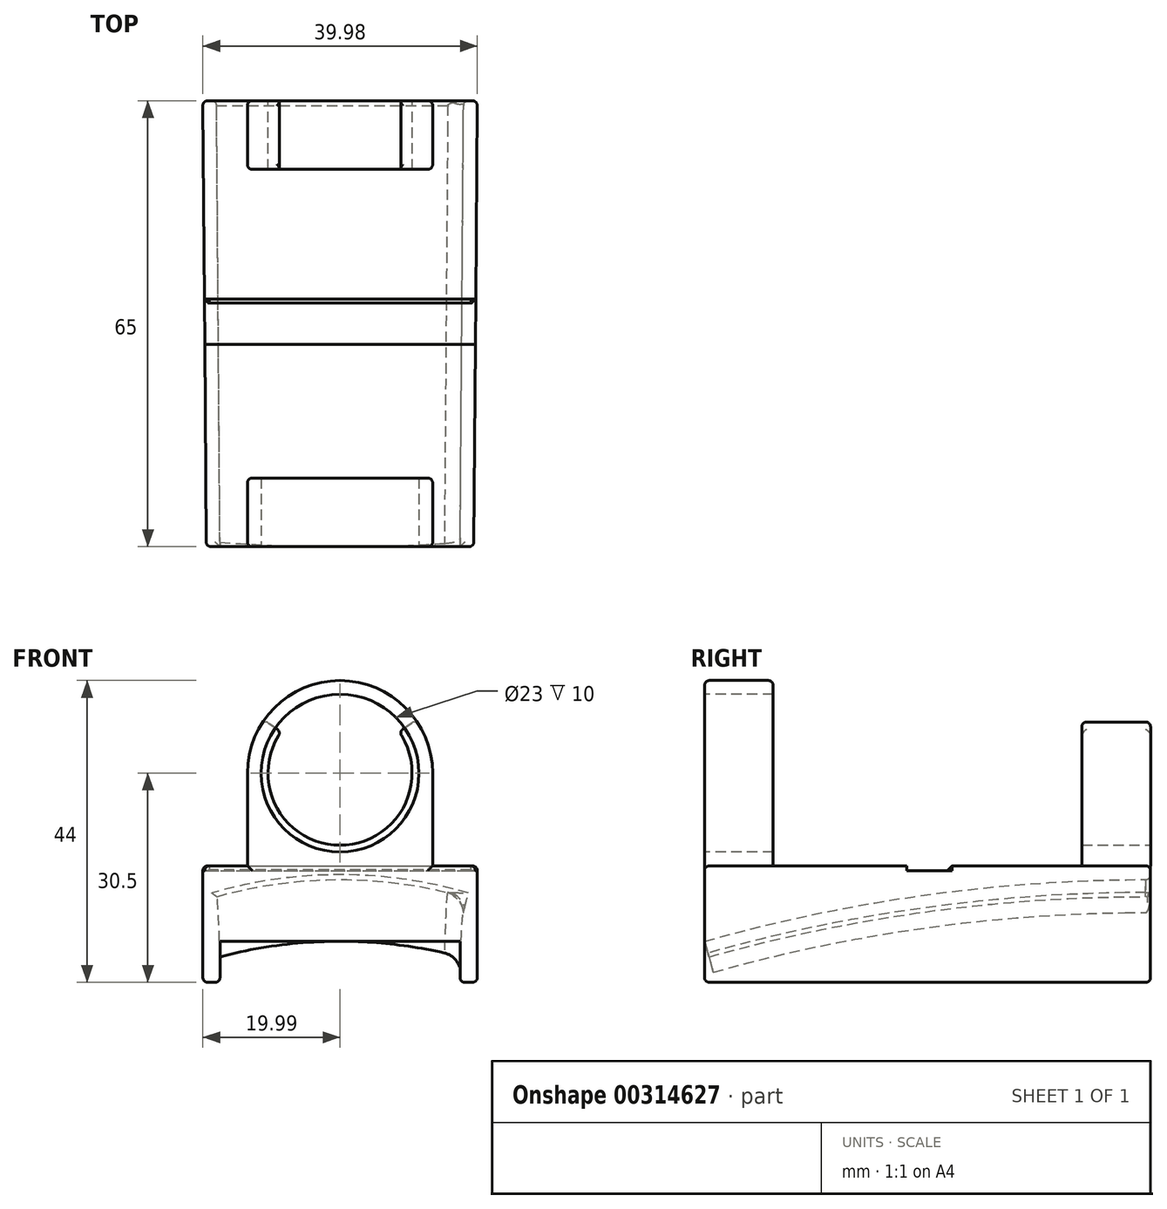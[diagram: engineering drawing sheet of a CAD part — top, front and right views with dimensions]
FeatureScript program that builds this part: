
annotation { "Feature Type Name" : "Feature", "Feature Type Description" : "" }
export const myFeature = defineFeature(function(context is Context, id is Id, definition is map)
    precondition{}
    {
        {
            assignVariable(context, id + "F0", {"name" : "var_thickness", "anyValue" : 2});
        }
        {
            var Q0;
            Q0=qCreatedBy(makeId("Top.planeOp"),FACE);
            var sketch = newSketch(context, id + "F1", { "sketchPlane" : qUnion([Q0])});
            skLineSegment(sketch, "E0.bottom", {"start": v(-20, 32.5) * mm, "end": v(20, 32.5) * mm});
            skLineSegment(sketch, "E0.top", {"start": v(-19.5, -32.5) * mm, "end": v(19.5, -32.5) * mm});
            skLineSegment(sketch, "E0.left", {"start": v(-20, 32.5) * mm, "end": v(-19.5, -32.5) * mm});
            skLineSegment(sketch, "E0.right", {"start": v(20, 32.5) * mm, "end": v(19.5, -32.5) * mm});
            skSolve(sketch);
        }
        {
            var Q0;
            Q0 = qSketchRegion(id + "F1", true);
            extrude(context, id + "F2", {"entities" : qUnion([Q0]), "depth" : 2 * mm});
        }
        {
            var Q0;
            Q0=makeQuery(id+"F2.opExtrude","CAP_FACE",FACE,{"disambiguationData":[OSD([sQuery(id+"F1.wireOp",EDGE,"E0.bottom"),sQuery(id+"F1.wireOp",EDGE,"E0.top"),sQuery(id+"F1.wireOp",EDGE,"E0.left"),sQuery(id+"F1.wireOp",EDGE,"E0.right")])],"isStart":true});
            var sketch = newSketch(context, id + "F3", { "sketchPlane" : qUnion([Q0])});
            skLineSegment(sketch, "E1", {"start": v(20, -32.5) * mm, "end": v(19.5, 32.5) * mm});
            skLineSegment(sketch, "E2", {"start": v(19.5, 32.5) * mm, "end": v(17.5, 32.5) * mm});
            skLineSegment(sketch, "E3", {"start": v(17.5, 32.5) * mm, "end": v(18, -32.5) * mm});
            skLineSegment(sketch, "E4", {"start": v(18, -32.5) * mm, "end": v(20, -32.5) * mm});
            skLineSegment(sketch, "E5", {"start": v(0, -32.5) * mm, "end": v(0, 32.5) * mm, "construction": true});
            skLineSegment(sketch, "E6.MirrorCS", {"start": v(-18, -32.5) * mm, "end": v(-20, -32.5) * mm});
            skLineSegment(sketch, "E7.MirrorCS", {"start": v(-17.5, 32.5) * mm, "end": v(-18, -32.5) * mm});
            skLineSegment(sketch, "E8.MirrorCS", {"start": v(-20, -32.5) * mm, "end": v(-19.5, 32.5) * mm});
            skLineSegment(sketch, "E9.MirrorCS", {"start": v(-19.5, 32.5) * mm, "end": v(-17.5, 32.5) * mm});
            skSolve(sketch);
        }
        {
            var Q0;
            Q0 = qSketchRegion(id + "F3", true);
            extrude(context, id + "F4", {"entities" : qUnion([Q0]), "operationType" : NewBodyOperationType.ADD, "depth" : 15 * mm});
        }
        {
            var Q0;
            Q0=makeQuery(id+"F2.opExtrude","CAP_FACE",FACE,{"disambiguationData":[OSD([sQuery(id+"F1.wireOp",EDGE,"E0.bottom"),sQuery(id+"F1.wireOp",EDGE,"E0.top"),sQuery(id+"F1.wireOp",EDGE,"E0.left"),sQuery(id+"F1.wireOp",EDGE,"E0.right")])],"isStart":false});
            var sketch = newSketch(context, id + "F5", { "sketchPlane" : qUnion([Q0])});
            skLineSegment(sketch, "E10.bottom", {"start": v(-13.5, -32.5) * mm, "end": v(13.5, -32.5) * mm});
            skLineSegment(sketch, "E10.top", {"start": v(-13.5, -22.5) * mm, "end": v(13.5, -22.5) * mm});
            skLineSegment(sketch, "E10.left", {"start": v(-13.5, -32.5) * mm, "end": v(-13.5, -22.5) * mm});
            skLineSegment(sketch, "E10.right", {"start": v(13.5, -32.5) * mm, "end": v(13.5, -22.5) * mm});
            skLineSegment(sketch, "E11.bottom", {"start": v(-13.5, 32.5) * mm, "end": v(13.5, 32.5) * mm});
            skLineSegment(sketch, "E11.top", {"start": v(-13.5, 22.5) * mm, "end": v(13.5, 22.5) * mm});
            skLineSegment(sketch, "E11.left", {"start": v(-13.5, 32.5) * mm, "end": v(-13.5, 22.5) * mm});
            skLineSegment(sketch, "E11.right", {"start": v(13.5, 32.5) * mm, "end": v(13.5, 22.5) * mm});
            skSolve(sketch);
        }
        {
            var Q0;
            Q0 = qSketchRegion(id + "F5", true);
            extrude(context, id + "F6", {"entities" : qUnion([Q0]), "operationType" : NewBodyOperationType.ADD, "depth" : (25 + getVariable(context, 'var_thickness')) * mm});
        }
        {
            var Q0;
            Q0=makeQuery(id+"F6.opExtrude","CAP_EDGE",EDGE,{"disambiguationData":[OSD([sQuery(id+"F5.wireOp",EDGE,"E10.right")])],"isStart":false});
            var Q1;
            Q1=makeQuery(id+"F6.opExtrude","CAP_EDGE",EDGE,{"disambiguationData":[OSD([sQuery(id+"F5.wireOp",EDGE,"E10.left")])],"isStart":false});
            var Q2;
            Q2=makeQuery(id+"F6.opExtrude","CAP_EDGE",EDGE,{"disambiguationData":[OSD([sQuery(id+"F5.wireOp",EDGE,"E11.right")])],"isStart":false});
            var Q3;
            Q3=makeQuery(id+"F6.opExtrude","CAP_EDGE",EDGE,{"disambiguationData":[OSD([sQuery(id+"F5.wireOp",EDGE,"E11.left")])],"isStart":false});
            fillet(context, id + "F7", {"entities" : qUnion([Q0, Q1, Q2, Q3]), "radius" : (11.5 + getVariable(context, 'var_thickness')) * mm, "tangentPropagation" : true, "allowEdgeOverflow" : false});
        }
        {
            var Q0;
            Q0=makeQuery(id+"F6.boolean.opBoolean","MERGE",FACE,{"derivedFrom":[makeQuery(id+"F4.boolean.opBoolean","MERGE",FACE,{"derivedFrom":[makeQuery(id+"F2.opExtrude","SWEPT_FACE",FACE,{"disambiguationData":[OSD([sQuery(id+"F1.wireOp",EDGE,"E0.top")])]}),makeQuery(id+"F4.opExtrude","SWEPT_FACE",FACE,{"disambiguationData":[OSD([sQuery(id+"F3.wireOp",EDGE,"E2")])]}),makeQuery(id+"F4.opExtrude","SWEPT_FACE",FACE,{"disambiguationData":[OSD([sQuery(id+"F3.wireOp",EDGE,"E9.MirrorCS")])]})]}),makeQuery(id+"F6.opExtrude","SWEPT_FACE",FACE,{"disambiguationData":[OSD([sQuery(id+"F5.wireOp",EDGE,"E10.bottom")])]})]});
            var sketch = newSketch(context, id + "F8", { "sketchPlane" : qUnion([Q0])});
            skCircle(sketch, "E12", {"center": v(0, 15.5) * mm, "radius": 11.5 * mm});
            skSolve(sketch);
        }
        {
            var Q0;
            Q0 = qSketchRegion(id + "F8", true);
            var Q1;
            Q1=makeQuery(id+"F6.opExtrude","SWEPT_FACE",FACE,{"disambiguationData":[OSD([sQuery(id+"F5.wireOp",EDGE,"E10.top")])]});
            var Q2;
            Q2=makeQuery(id+"F6.opExtrude","SWEPT_FACE",FACE,{"disambiguationData":[OSD([sQuery(id+"F5.wireOp",EDGE,"E10.top")])]});
            extrude(context, id + "F9", {"entities" : qUnion([Q0, Q1]), "operationType" : NewBodyOperationType.REMOVE, "endBound" : BoundingType.UP_TO_NEXT, "oppositeDirection" : true, "endBoundEntityFace" : qUnion([Q2]), "depth" : 25 * mm});
        }
        {
            var Q0;
            Q0=makeQuery(id+"F6.opExtrude","SWEPT_FACE",FACE,{"disambiguationData":[OSD([sQuery(id+"F5.wireOp",EDGE,"E11.bottom")])]});
            var sketch = newSketch(context, id + "F10", { "sketchPlane" : qUnion([Q0])});
            skCircle(sketch, "E13", {"center": v(0, 15.5) * mm, "radius": 10.5 * mm});
            skSolve(sketch);
        }
        {
            var Q0;
            Q0 = qSketchRegion(id + "F10", true);
            extrude(context, id + "F11", {"entities" : qUnion([Q0]), "operationType" : NewBodyOperationType.REMOVE, "endBound" : BoundingType.UP_TO_NEXT, "oppositeDirection" : true, "depth" : 25 * mm});
        }
        {
            var Q0;
            Q0=makeQuery(id+"F6.opExtrude","SWEPT_FACE",FACE,{"disambiguationData":[OSD([sQuery(id+"F5.wireOp",EDGE,"E11.bottom")])]});
            var sketch = newSketch(context, id + "F12", { "sketchPlane" : qUnion([Q0])});
            skArc(sketch, "E14", {"start": v(4.1, 18.37) * mm, "mid": v(0, 20.5) * mm, "end": v(-4.1, 18.37) * mm});
            skArc(sketch, "E15", {"start": v(12.29, 24.1) * mm, "mid": v(0, 30.5) * mm, "end": v(-12.29, 24.1) * mm});
            skLineSegment(sketch, "E16", {"start": v(4.1, 18.37) * mm, "end": v(12.29, 24.1) * mm});
            skLineSegment(sketch, "E17", {"start": v(-12.29, 24.1) * mm, "end": v(-4.1, 18.37) * mm});
            skSolve(sketch);
        }
        {
            var Q0;
            Q0 = qSketchRegion(id + "F12", true);
            var Q1;
            Q1=makeQuery(id+"F6.opExtrude","SWEPT_FACE",FACE,{"disambiguationData":[OSD([sQuery(id+"F5.wireOp",EDGE,"E11.top")])]});
            extrude(context, id + "F13", {"entities" : qUnion([Q0]), "operationType" : NewBodyOperationType.REMOVE, "endBound" : BoundingType.UP_TO_SURFACE, "oppositeDirection" : true, "endBoundEntityFace" : qUnion([Q1]), "depth" : 25 * mm});
        }
        {
            var Q0;
            Q0=qCreatedBy(makeId("Right.planeOp"),FACE);
            var sketch = newSketch(context, id + "F14", { "sketchPlane" : qUnion([Q0])});
            skLineSegment(sketch, "E18", {"start": v(32.5, 0) * mm, "end": v(-32.5, 0) * mm});
            skLineSegment(sketch, "E19", {"start": v(-32.5, 0) * mm, "end": v(-32.5, -9) * mm});
            skArc(sketch, "E20", {"start": v(32.5, 0) * mm, "mid": v(-0.31, -2.26) * mm, "end": v(-32.5, -9) * mm});
            skSolve(sketch);
        }
        {
            var Q0;
            Q0 = qSketchRegion(id + "F14", true);
            extrude(context, id + "F15", {"entities" : qUnion([Q0]), "operationType" : NewBodyOperationType.ADD, "endBound" : BoundingType.SYMMETRIC, "depth" : 37 * mm});
        }
        {
            var Q0;
            Q0=qCreatedBy(makeId("Right.planeOp"),FACE);
            var sketch = newSketch(context, id + "F16", { "sketchPlane" : qUnion([Q0])});
            skArc(sketch, "E21", {"start": v(32.5, 0) * mm, "mid": v(-0.31, -2.26) * mm, "end": v(-32.5, -9) * mm});
            skSolve(sketch);
        }
        {
            var Q0;
            Q0=makeQuery(id+"F4.boolean.opBoolean","MERGE",FACE,{"derivedFrom":[makeQuery(id+"F2.opExtrude","SWEPT_FACE",FACE,{"disambiguationData":[OSD([sQuery(id+"F1.wireOp",EDGE,"E0.bottom")])]}),makeQuery(id+"F4.opExtrude","SWEPT_FACE",FACE,{"disambiguationData":[OSD([sQuery(id+"F3.wireOp",EDGE,"E4")])]}),makeQuery(id+"F4.opExtrude","SWEPT_FACE",FACE,{"disambiguationData":[OSD([sQuery(id+"F3.wireOp",EDGE,"E6.MirrorCS")])]})]});
            var sketch = newSketch(context, id + "F17", { "sketchPlane" : qUnion([Q0])});
            skLineSegment(sketch, "E22", {"start": v(18, -2.5) * mm, "end": v(18, 0) * mm});
            skLineSegment(sketch, "E23", {"start": v(18, 0) * mm, "end": v(-18, 0) * mm});
            skLineSegment(sketch, "E24", {"start": v(-18, 0) * mm, "end": v(-18, -2.5) * mm});
            skArc(sketch, "E25", {"start": v(18, -2.5) * mm, "mid": v(0, 0) * mm, "end": v(-18, -2.5) * mm});
            skSolve(sketch);
        }
        {
            var Q0;
            Q0 = qSketchRegion(id + "F17", true);
            var Q1;
            Q1=sQuery(id+"F16.wireOp",EDGE,"E21");
            sweep(context, id + "F18", {"operationType" : NewBodyOperationType.ADD, "profiles" : qUnion([Q0]), "path" : qUnion([Q1])});
        }
        {
            var Q0;
            Q0=qCreatedBy(makeId("Right.planeOp"),FACE);
            var sketch = newSketch(context, id + "F19", { "sketchPlane" : qUnion([Q0])});
            skLineSegment(sketch, "E26.bottom", {"start": v(-3, 2) * mm, "end": v(3, 2) * mm});
            skLineSegment(sketch, "E26.top", {"start": v(-3, 1.25) * mm, "end": v(3, 1.25) * mm});
            skLineSegment(sketch, "E26.left", {"start": v(-3, 2) * mm, "end": v(-3, 1.25) * mm});
            skLineSegment(sketch, "E26.right", {"start": v(3, 2) * mm, "end": v(3, 1.25) * mm});
            skSolve(sketch);
        }
        {
            var Q0;
            Q0 = qSketchRegion(id + "F19", true);
            extrude(context, id + "F20", {"entities" : qUnion([Q0]), "operationType" : NewBodyOperationType.REMOVE, "endBound" : BoundingType.SYMMETRIC, "oppositeDirection" : true, "depth" : 50 * mm});
        }
        {
            var Q0;
            Q0=makeQuery(id+"F4.opExtrude","CAP_FACE",FACE,{"disambiguationData":[OSD([sQuery(id+"F3.wireOp",EDGE,"E1"),sQuery(id+"F3.wireOp",EDGE,"E2"),sQuery(id+"F3.wireOp",EDGE,"E3"),sQuery(id+"F3.wireOp",EDGE,"E4")])],"isStart":false});
            var Q1;
            Q1=makeQuery(id+"F4.opExtrude","CAP_FACE",FACE,{"disambiguationData":[OSD([sQuery(id+"F3.wireOp",EDGE,"E6.MirrorCS"),sQuery(id+"F3.wireOp",EDGE,"E7.MirrorCS"),sQuery(id+"F3.wireOp",EDGE,"E8.MirrorCS"),sQuery(id+"F3.wireOp",EDGE,"E9.MirrorCS")])],"isStart":false});
            var Q2;
            Q2=makeQuery(id+"F7.opFillet","BLEND_EDGE",EDGE,{"blendedFrom":[makeQuery(id+"F6.opExtrude","CAP_EDGE",EDGE,{"disambiguationData":[OSD([sQuery(id+"F5.wireOp",EDGE,"E10.left")])],"isStart":false}),makeQuery(id+"F6.boolean.opBoolean","MERGE",FACE,{"derivedFrom":[makeQuery(id+"F4.boolean.opBoolean","MERGE",FACE,{"derivedFrom":[makeQuery(id+"F2.opExtrude","SWEPT_FACE",FACE,{"disambiguationData":[OSD([sQuery(id+"F1.wireOp",EDGE,"E0.top")])]}),makeQuery(id+"F4.opExtrude","SWEPT_FACE",FACE,{"disambiguationData":[OSD([sQuery(id+"F3.wireOp",EDGE,"E2")])]}),makeQuery(id+"F4.opExtrude","SWEPT_FACE",FACE,{"disambiguationData":[OSD([sQuery(id+"F3.wireOp",EDGE,"E9.MirrorCS")])]})]}),makeQuery(id+"F6.opExtrude","SWEPT_FACE",FACE,{"disambiguationData":[OSD([sQuery(id+"F5.wireOp",EDGE,"E10.bottom")])]})]})],"blendedInto":[makeQuery(id+"F6.boolean.opBoolean","MERGE",FACE,{"derivedFrom":[makeQuery(id+"F4.boolean.opBoolean","MERGE",FACE,{"derivedFrom":[makeQuery(id+"F2.opExtrude","SWEPT_FACE",FACE,{"disambiguationData":[OSD([sQuery(id+"F1.wireOp",EDGE,"E0.top")])]}),makeQuery(id+"F4.opExtrude","SWEPT_FACE",FACE,{"disambiguationData":[OSD([sQuery(id+"F3.wireOp",EDGE,"E2")])]}),makeQuery(id+"F4.opExtrude","SWEPT_FACE",FACE,{"disambiguationData":[OSD([sQuery(id+"F3.wireOp",EDGE,"E9.MirrorCS")])]})]}),makeQuery(id+"F6.opExtrude","SWEPT_FACE",FACE,{"disambiguationData":[OSD([sQuery(id+"F5.wireOp",EDGE,"E10.bottom")])]})]})]});
            var Q3;
            Q3=makeQuery(id+"F7.opFillet","BLEND_EDGE",EDGE,{"blendedFrom":[makeQuery(id+"F6.opExtrude","CAP_EDGE",EDGE,{"disambiguationData":[OSD([sQuery(id+"F5.wireOp",EDGE,"E10.left")])],"isStart":false}),makeQuery(id+"F6.opExtrude","SWEPT_FACE",FACE,{"disambiguationData":[OSD([sQuery(id+"F5.wireOp",EDGE,"E10.top")])]})],"blendedInto":[makeQuery(id+"F6.opExtrude","SWEPT_FACE",FACE,{"disambiguationData":[OSD([sQuery(id+"F5.wireOp",EDGE,"E10.top")])]})]});
            var Q4;
            {var subQ0=sQuery(id+"F1.wireOp",EDGE,"E0.right");var subQ1=sQuery(id+"F1.wireOp",EDGE,"E0.top");Q4=makeQuery(id+"F6.boolean.opBoolean","SPLIT",EDGE,{"disambiguationData":[TD([makeQuery(id+"F2.opExtrude","SWEPT_FACE",FACE,{"disambiguationData":[OSD([subQ0])]})])],"derivedFrom":makeQuery(id+"F2.opExtrude","CAP_EDGE",EDGE,{"disambiguationData":[OSD([subQ1])],"isStart":false})});}
            var Q5;
            {var subQ0=sQuery(id+"F1.wireOp",EDGE,"E0.left");var subQ1=sQuery(id+"F1.wireOp",EDGE,"E0.top");Q5=makeQuery(id+"F6.boolean.opBoolean","SPLIT",EDGE,{"disambiguationData":[TD([makeQuery(id+"F2.opExtrude","SWEPT_FACE",FACE,{"disambiguationData":[OSD([subQ0])]})])],"derivedFrom":makeQuery(id+"F2.opExtrude","CAP_EDGE",EDGE,{"disambiguationData":[OSD([subQ1])],"isStart":false})});}
            var Q6;
            Q6=makeQuery(id+"F4.boolean.opBoolean","MERGE",EDGE,{"derivedFrom":[makeQuery(id+"F2.opExtrude","SWEPT_EDGE",EDGE,{"disambiguationData":[OSD([sQuery(id+"F1.wireOp",EDGE,"E0.top"),sQuery(id+"F1.wireOp",EDGE,"E0.left")])]}),makeQuery(id+"F4.opExtrude","SWEPT_EDGE",EDGE,{"disambiguationData":[OSD([sQuery(id+"F3.wireOp",EDGE,"E8.MirrorCS"),sQuery(id+"F3.wireOp",EDGE,"E9.MirrorCS")])]})]});
            var Q7;
            Q7=makeQuery(id+"F4.boolean.opBoolean","MERGE",EDGE,{"derivedFrom":[makeQuery(id+"F2.opExtrude","SWEPT_EDGE",EDGE,{"disambiguationData":[OSD([sQuery(id+"F1.wireOp",EDGE,"E0.top"),sQuery(id+"F1.wireOp",EDGE,"E0.right")])]}),makeQuery(id+"F4.opExtrude","SWEPT_EDGE",EDGE,{"disambiguationData":[OSD([sQuery(id+"F3.wireOp",EDGE,"E1"),sQuery(id+"F3.wireOp",EDGE,"E2")])]})]});
            var Q8;
            Q8=makeQuery(id+"F13.boolean.opBoolean","COPY",FACE,{"derivedFrom":makeQuery(id+"F13.opExtrude","SWEPT_FACE",FACE,{"disambiguationData":[OSD([sQuery(id+"F12.wireOp",EDGE,"E17")])]})});
            var Q9;
            Q9=makeQuery(id+"F13.boolean.opBoolean","COPY",FACE,{"derivedFrom":makeQuery(id+"F13.opExtrude","SWEPT_FACE",FACE,{"disambiguationData":[OSD([sQuery(id+"F12.wireOp",EDGE,"E16")])]})});
            var Q10;
            Q10=makeQuery(id+"F7.opFillet","BLEND_EDGE",EDGE,{"blendedFrom":[makeQuery(id+"F6.opExtrude","CAP_EDGE",EDGE,{"disambiguationData":[OSD([sQuery(id+"F5.wireOp",EDGE,"E11.right")])],"isStart":false}),makeQuery(id+"F6.opExtrude","SWEPT_FACE",FACE,{"disambiguationData":[OSD([sQuery(id+"F5.wireOp",EDGE,"E11.bottom")])]})],"blendedInto":[makeQuery(id+"F6.opExtrude","SWEPT_FACE",FACE,{"disambiguationData":[OSD([sQuery(id+"F5.wireOp",EDGE,"E11.bottom")])]})]});
            var Q11;
            {var subQ1=makeQuery(id+"F6.opExtrude","SWEPT_FACE",FACE,{"disambiguationData":[OSD([sQuery(id+"F5.wireOp",EDGE,"E11.bottom")])]});var subQ2=makeQuery(id+"F9.opExtrude","SWEPT_FACE",FACE,{"disambiguationData":[OSD([sQuery(id+"F8.wireOp",EDGE,"E12")])]});Q11=makeQuery(id+"F13.boolean.opBoolean","SPLIT",EDGE,{"disambiguationData":[TD([makeQuery(id+"F13.opExtrude","SWEPT_FACE",FACE,{"disambiguationData":[OSD([sQuery(id+"F12.wireOp",EDGE,"E17")])]})])],"derivedFrom":makeQuery(id+"F9.boolean.opBoolean","INTERSECT",EDGE,{"derivedFrom":[subQ1,subQ2]})});}
            var Q12;
            Q12=makeQuery(id+"F7.opFillet","BLEND_EDGE",EDGE,{"blendedFrom":[makeQuery(id+"F6.opExtrude","CAP_EDGE",EDGE,{"disambiguationData":[OSD([sQuery(id+"F5.wireOp",EDGE,"E11.left")])],"isStart":false}),makeQuery(id+"F6.opExtrude","SWEPT_FACE",FACE,{"disambiguationData":[OSD([sQuery(id+"F5.wireOp",EDGE,"E11.bottom")])]})],"blendedInto":[makeQuery(id+"F6.opExtrude","SWEPT_FACE",FACE,{"disambiguationData":[OSD([sQuery(id+"F5.wireOp",EDGE,"E11.bottom")])]})]});
            var Q13;
            Q13=makeQuery(id+"F7.opFillet","BLEND_EDGE",EDGE,{"blendedFrom":[makeQuery(id+"F6.opExtrude","CAP_EDGE",EDGE,{"disambiguationData":[OSD([sQuery(id+"F5.wireOp",EDGE,"E11.left")])],"isStart":false}),makeQuery(id+"F6.opExtrude","SWEPT_FACE",FACE,{"disambiguationData":[OSD([sQuery(id+"F5.wireOp",EDGE,"E11.top")])]})],"blendedInto":[makeQuery(id+"F6.opExtrude","SWEPT_FACE",FACE,{"disambiguationData":[OSD([sQuery(id+"F5.wireOp",EDGE,"E11.top")])]})]});
            var Q14;
            Q14=makeQuery(id+"F7.opFillet","BLEND_EDGE",EDGE,{"blendedFrom":[makeQuery(id+"F6.opExtrude","CAP_EDGE",EDGE,{"disambiguationData":[OSD([sQuery(id+"F5.wireOp",EDGE,"E11.right")])],"isStart":false}),makeQuery(id+"F6.opExtrude","SWEPT_FACE",FACE,{"disambiguationData":[OSD([sQuery(id+"F5.wireOp",EDGE,"E11.top")])]})],"blendedInto":[makeQuery(id+"F6.opExtrude","SWEPT_FACE",FACE,{"disambiguationData":[OSD([sQuery(id+"F5.wireOp",EDGE,"E11.top")])]})]});
            var Q15;
            {var subQ1=makeQuery(id+"F6.opExtrude","SWEPT_FACE",FACE,{"disambiguationData":[OSD([sQuery(id+"F5.wireOp",EDGE,"E11.top")])]});var subQ2=makeQuery(id+"F9.opExtrude","SWEPT_FACE",FACE,{"disambiguationData":[OSD([sQuery(id+"F8.wireOp",EDGE,"E12")])]});Q15=makeQuery(id+"F13.boolean.opBoolean","SPLIT",EDGE,{"disambiguationData":[TD([makeQuery(id+"F13.opExtrude","SWEPT_FACE",FACE,{"disambiguationData":[OSD([sQuery(id+"F12.wireOp",EDGE,"E17")])]})])],"derivedFrom":makeQuery(id+"F9.boolean.opBoolean","INTERSECT",EDGE,{"derivedFrom":[subQ1,subQ2]})});}
            var Q16;
            Q16=makeQuery(id+"F4.opExtrude","CAP_EDGE",EDGE,{"disambiguationData":[OSD([sQuery(id+"F3.wireOp",EDGE,"E3")])],"isStart":true});
            var Q17;
            Q17=makeQuery(id+"F4.opExtrude","CAP_EDGE",EDGE,{"disambiguationData":[OSD([sQuery(id+"F3.wireOp",EDGE,"E7.MirrorCS")])],"isStart":true});
            var Q18;
            Q18=makeQuery(id+"F4.boolean.opBoolean","MERGE",FACE,{"derivedFrom":[makeQuery(id+"F2.opExtrude","SWEPT_FACE",FACE,{"disambiguationData":[OSD([sQuery(id+"F1.wireOp",EDGE,"E0.bottom")])]}),makeQuery(id+"F4.opExtrude","SWEPT_FACE",FACE,{"disambiguationData":[OSD([sQuery(id+"F3.wireOp",EDGE,"E4")])]}),makeQuery(id+"F4.opExtrude","SWEPT_FACE",FACE,{"disambiguationData":[OSD([sQuery(id+"F3.wireOp",EDGE,"E6.MirrorCS")])]})]});
            var Q19;
            Q19=makeQuery(id+"F2.opExtrude","CAP_EDGE",EDGE,{"disambiguationData":[OSD([sQuery(id+"F1.wireOp",EDGE,"E0.left")])],"isStart":false});
            var Q20;
            Q20=makeQuery(id+"F2.opExtrude","CAP_EDGE",EDGE,{"disambiguationData":[OSD([sQuery(id+"F1.wireOp",EDGE,"E0.right")])],"isStart":false});
            fillet(context, id + "F21", {"entities" : qUnion([Q0, Q1, Q2, Q3, Q4, Q5, Q6, Q7, Q8, Q9, Q10, Q11, Q12, Q13, Q14, Q15, Q16, Q17, Q18, Q19, Q20]), "radius" : 0.7 * mm, "tangentPropagation" : true, "allowEdgeOverflow" : false});
        }
        {
            var Q0;
            Q0=makeQuery(id+"F20.boolean.opBoolean","COPY",EDGE,{"derivedFrom":makeQuery(id+"F20.opExtrude","SWEPT_EDGE",EDGE,{"disambiguationData":[OSD([sQuery(id+"F19.wireOp",EDGE,"E26.bottom"),sQuery(id+"F19.wireOp",EDGE,"E26.left")])]})});
            var Q1;
            Q1=makeQuery(id+"F20.boolean.opBoolean","COPY",EDGE,{"derivedFrom":makeQuery(id+"F20.opExtrude","SWEPT_EDGE",EDGE,{"disambiguationData":[OSD([sQuery(id+"F19.wireOp",EDGE,"E26.bottom"),sQuery(id+"F19.wireOp",EDGE,"E26.right")])]})});
            chamfer(context, id + "F22", {"entities" : qUnion([Q0, Q1]), "width" : 0.6 * mm, "tangentPropagation" : true});
        }
        {
            var Q0;
            {var subQ0=sQuery(id+"F17.wireOp",EDGE,"E25");var subQ1=sQuery(id+"F3.wireOp",EDGE,"E7.MirrorCS");var subQ2=sQuery(id+"F16.wireOp",EDGE,"E21");Q0=makeQuery(id+"F18.boolean.opBoolean","INTERSECT",EDGE,{"derivedFrom":[makeQuery(id+"F4.opExtrude","SWEPT_FACE",FACE,{"disambiguationData":[OSD([subQ1])]}),makeQuery(id+"F18.opSweep","SWEPT_FACE",FACE,{"disambiguationData":[OSD([subQ2,subQ0]),TDD([subQ2,makeQuery(id+"F17.imprint","IMPRINT",EDGE,{"disambiguationData":[TD([[makeQuery(id+"F17.imprint","INTERSECT",VERTEX,{"derivedFrom":[sQuery(id+"F17.wireOp",EDGE,"E23"),subQ0]}),1.0]])],"derivedFrom":subQ0})])]})]});}
            var Q1;
            {var subQ0=sQuery(id+"F17.wireOp",EDGE,"E25");var subQ1=sQuery(id+"F3.wireOp",EDGE,"E3");var subQ3=makeQuery(id+"F17.imprint","INTERSECT",VERTEX,{"derivedFrom":[sQuery(id+"F17.wireOp",EDGE,"E23"),subQ0]});var subQ4=sQuery(id+"F16.wireOp",EDGE,"E21");Q1=makeQuery(id+"F18.boolean.opBoolean","INTERSECT",EDGE,{"derivedFrom":[makeQuery(id+"F4.opExtrude","SWEPT_FACE",FACE,{"disambiguationData":[OSD([subQ1])]}),makeQuery(id+"F18.opSweep","SWEPT_FACE",FACE,{"disambiguationData":[OSD([subQ4,subQ0]),TDD([subQ4,makeQuery(id+"F17.imprint","IMPRINT",EDGE,{"disambiguationData":[TD([[subQ3,1.0]])],"derivedFrom":subQ0})])]}),makeQuery(id+"F18.opSweep","SWEPT_FACE",FACE,{"disambiguationData":[OSD([subQ4,subQ0]),TDD([subQ4,makeQuery(id+"F17.imprint","IMPRINT",EDGE,{"disambiguationData":[TD([[subQ3,-1.0]])],"derivedFrom":subQ0})])]})]});}
            fillet(context, id + "F23", {"entities" : qUnion([Q0, Q1]), "radius" : 3 * mm, "tangentPropagation" : true, "allowEdgeOverflow" : false});
        }
    });
